# Revit family: Gira_021524
name_source: partatom
category: Electrical Fixtures
revit_build: Autodesk Revit 2017 (Build: 20160225_1515(x64)
units: mm (PartAtom-declared; Revit-internal decimal feet)

## family parameters
Cut with Voids When Loaded = No
Host = Face
Maintain Annotation Orientation = No
Part Type = Normal
Room Calculation Point = No
Round Connector Dimension = Use Diameter
Shared = No

## types (1)
- Abdeckrahmen 5f Zwischenr. AN Gira Event Opak Weiß
    Anzahl der Einheiten = 5
    Anzahl der Einheiten horizontal = 5
    Anzahl der Einheiten vertikal = 5
    Available = Yes
    Befestigungsart = Klemmbefestigung
    Category = Abdeckrahmen
    Data sheet (1) = https://katalog.gira.de
    Default Elevation = 1219 mm
    Farbe = weiß
    GTIN = 4010337215240
    Geeignet für Einbauinstallation = No
    Geeignet für Geräteeinbaukanal = No
    Geeignet für Unterflurkanaldose = No
    Geeignet für Unterputz-Installation = Yes
    HAN = 021524
    Halogenfrei = Yes
    HeinzeBIM = https://bimportal.heinze.de
    Keynote = Event_Rahmen_5fach
    Manufacturer URL = https://www.gira.de
    Mit Klappdeckel = No
    Mit Montagerahmen = No
    Montagerichtung = horizontal und vertikal
    Name = Abdeckrahmen 5f Zwischenr. AN Gira Event Opak Weiß
    Oberfläche = sonstige
    Region = DE
    Schutzart (IP) = IP20
    Textfeld/Beschriftungsfläche = No
    Transparent = No
    URL = http://katalog.gira.de
    Werkstoff = Kunststoff
    Werkstoffgüte = Thermoplast

## geometry (parser evidence)
native form markers: Blend x2, Sweep x3
no freeform markers — native parametric forms only
